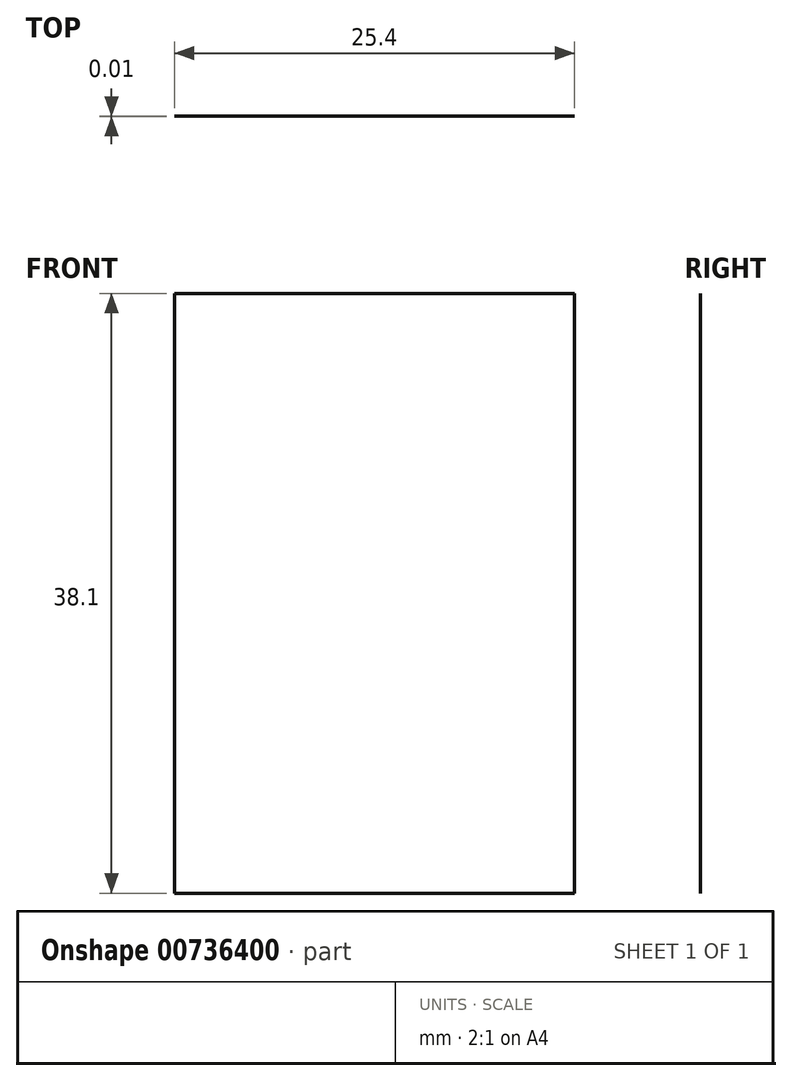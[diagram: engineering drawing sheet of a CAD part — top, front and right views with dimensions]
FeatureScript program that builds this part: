
annotation { "Feature Type Name" : "Feature", "Feature Type Description" : "" }
export const myFeature = defineFeature(function(context is Context, id is Id, definition is map)
    precondition{}
    {
        {
            var Q0;
            Q0=qCreatedBy(makeId("Front.planeOp"),FACE);
            var sketch = newSketch(context, id + "F0", { "sketchPlane" : qUnion([Q0])});
            skLineSegment(sketch, "E0.bottom", {"start": v(0, 0) * mm, "end": v(25.4, 0) * mm});
            skLineSegment(sketch, "E0.top", {"start": v(0, 38.1) * mm, "end": v(25.4, 38.1) * mm});
            skLineSegment(sketch, "E0.left", {"start": v(0, 0) * mm, "end": v(0, 38.1) * mm});
            skLineSegment(sketch, "E0.right", {"start": v(25.4, 0) * mm, "end": v(25.4, 38.1) * mm});
            skSolve(sketch);
        }
        {
            var Q0;
            Q0=makeQuery(id+"F0.imprint","IMPRINT",FACE,{"disambiguationData":[TD([[makeQuery(id+"F0.imprint","IMPRINT",EDGE,{"derivedFrom":sQuery(id+"F0.wireOp",EDGE,"E0.bottom")}),1.0]])]});
            extrude(context, id + "F1", {"entities" : qUnion([Q0]), "depth" : 3 / 406.4 * mm, "offsetDistance" : 25.4 * mm});
        }
    });
